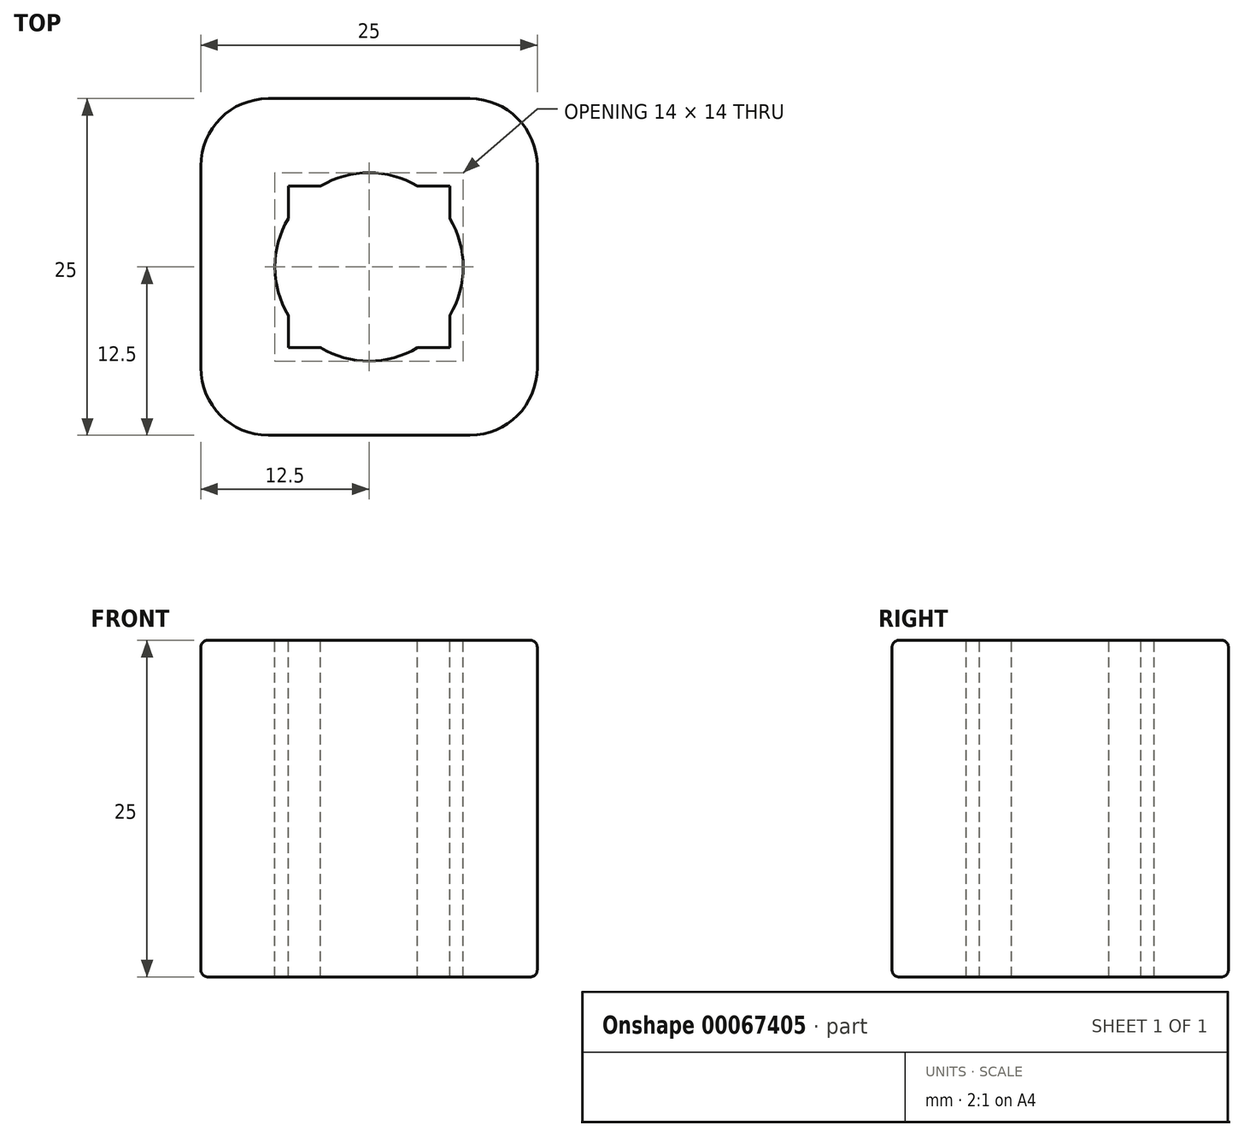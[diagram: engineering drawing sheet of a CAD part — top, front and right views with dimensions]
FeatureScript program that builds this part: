
annotation { "Feature Type Name" : "Feature", "Feature Type Description" : "" }
export const myFeature = defineFeature(function(context is Context, id is Id, definition is map)
    precondition{}
    {
        {
            var Q0;
            Q0=qCreatedBy(makeId("Top.planeOp"),FACE);
            var sketch = newSketch(context, id + "F0", { "sketchPlane" : qUnion([Q0])});
            skLineSegment(sketch, "E0.bottom", {"start": v(7.5, 12.5) * mm, "end": v(-7.5, 12.5) * mm});
            skLineSegment(sketch, "E0.top", {"start": v(7.5, -12.5) * mm, "end": v(-7.5, -12.5) * mm});
            skLineSegment(sketch, "E0.left", {"start": v(12.5, 7.5) * mm, "end": v(12.5, -7.5) * mm});
            skLineSegment(sketch, "E0.right", {"start": v(-12.5, 7.5) * mm, "end": v(-12.5, -7.5) * mm});
            skPoint(sketch, "E0.middle", {"position": v(0, 0) * mm});
            skPoint(sketch, "E1.visualSharp", {"position": v(12.5, -12.5) * mm});
            skArc(sketch, "E1.filletArc", {"start": v(7.5, -12.5) * mm, "mid": v(11.04, -11.04) * mm, "end": v(12.5, -7.5) * mm});
            skPoint(sketch, "E2.visualSharp", {"position": v(12.5, 12.5) * mm});
            skArc(sketch, "E2.filletArc", {"start": v(12.5, 7.5) * mm, "mid": v(11.04, 11.04) * mm, "end": v(7.5, 12.5) * mm});
            skPoint(sketch, "E3.visualSharp", {"position": v(-12.5, -12.5) * mm});
            skArc(sketch, "E3.filletArc", {"start": v(-12.5, -7.5) * mm, "mid": v(-11.04, -11.04) * mm, "end": v(-7.5, -12.5) * mm});
            skPoint(sketch, "E4.visualSharp", {"position": v(-12.5, 12.5) * mm});
            skArc(sketch, "E4.filletArc", {"start": v(-7.5, 12.5) * mm, "mid": v(-11.04, 11.04) * mm, "end": v(-12.5, 7.5) * mm});
            skSolve(sketch);
        }
        {
            var Q0;
            Q0 = qSketchRegion(id + "F0", true);
            extrude(context, id + "F1", {"entities" : qUnion([Q0]), "endBound" : BoundingType.SYMMETRIC, "depth" : 25 * mm});
        }
        {
            var Q0;
            Q0=makeQuery(id+"F1.opExtrude","CAP_EDGE",EDGE,{"disambiguationData":[OSD([sQuery(id+"F0.wireOp",EDGE,"E0.top")])],"isStart":true});
            var Q1;
            Q1=makeQuery(id+"F1.opExtrude","CAP_EDGE",EDGE,{"disambiguationData":[OSD([sQuery(id+"F0.wireOp",EDGE,"E0.right")])],"isStart":false});
            fillet(context, id + "F2", {"entities" : qUnion([Q0, Q1]), "radius" : 0.5 * mm, "tangentPropagation" : true, "allowEdgeOverflow" : false});
        }
        {
            var Q0;
            Q0=makeQuery(id+"F1.opExtrude","CAP_FACE",FACE,{"disambiguationData":[OSD([sQuery(id+"F0.wireOp",EDGE,"E0.bottom"),sQuery(id+"F0.wireOp",EDGE,"E0.top"),sQuery(id+"F0.wireOp",EDGE,"E0.left"),sQuery(id+"F0.wireOp",EDGE,"E0.right"),sQuery(id+"F0.wireOp",EDGE,"E1.filletArc"),sQuery(id+"F0.wireOp",EDGE,"E2.filletArc"),sQuery(id+"F0.wireOp",EDGE,"E3.filletArc"),sQuery(id+"F0.wireOp",EDGE,"E4.filletArc")])],"isStart":false});
            var sketch = newSketch(context, id + "F3", { "sketchPlane" : qUnion([Q0])});
            skLineSegment(sketch, "E5.bottom", {"start": v(6, -6) * mm, "end": v(-6, -6) * mm});
            skLineSegment(sketch, "E5.top", {"start": v(6, 6) * mm, "end": v(-6, 6) * mm});
            skLineSegment(sketch, "E5.left", {"start": v(6, -6) * mm, "end": v(6, 6) * mm});
            skLineSegment(sketch, "E5.right", {"start": v(-6, -6) * mm, "end": v(-6, 6) * mm});
            skPoint(sketch, "E5.middle", {"position": v(0, 0) * mm});
            skPoint(sketch, "E5.middle.positionSnap0", {"position": v(12, 0) * mm});
            skPoint(sketch, "E5.middle.positionSnap1", {"position": v(0, 12) * mm});
            skPoint(sketch, "E5.centerSnap0", {"position": v(12, 0) * mm});
            skPoint(sketch, "E5.centerSnap1", {"position": v(0, 12) * mm});
            skCircle(sketch, "E6", {"center": v(0, 0) * mm, "radius": 7 * mm});
            skSolve(sketch);
        }
        {
            var Q0;
            Q0 = qSketchRegion(id + "F3", true);
            extrude(context, id + "F4", {"entities" : qUnion([Q0]), "operationType" : NewBodyOperationType.REMOVE, "endBound" : BoundingType.THROUGH_ALL, "oppositeDirection" : true, "depth" : 25 * mm});
        }
    });
